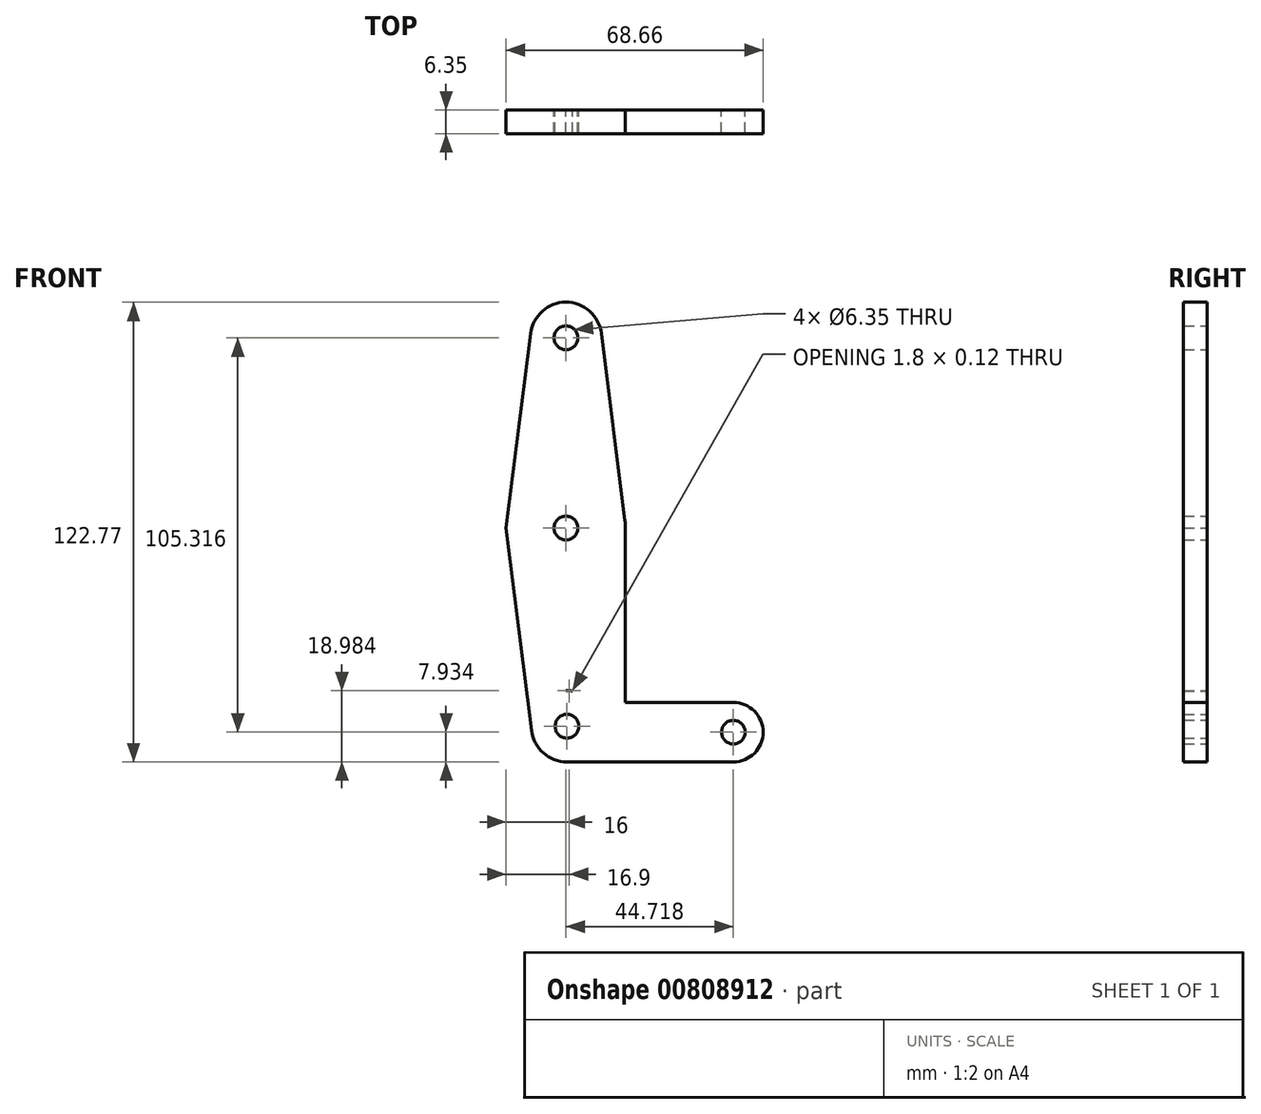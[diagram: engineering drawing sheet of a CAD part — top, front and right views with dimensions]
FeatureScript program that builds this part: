
annotation { "Feature Type Name" : "Feature", "Feature Type Description" : "" }
export const myFeature = defineFeature(function(context is Context, id is Id, definition is map)
    precondition{}
    {
        {
            var Q0;
            Q0=qCreatedBy(makeId("Front.planeOp"),FACE);
            var sketch = newSketch(context, id + "F0", { "sketchPlane" : qUnion([Q0])});
            skCircle(sketch, "E0", {"center": v(0, 0) * mm, "radius": 3.18 * mm});
            skCircle(sketch, "E1", {"center": v(0, 0) * mm, "radius": 15.88 * mm});
            skCircle(sketch, "E2", {"center": v(0, 50.8) * mm, "radius": 3.18 * mm});
            skCircle(sketch, "E3", {"center": v(0, 50.8) * mm, "radius": 9.53 * mm});
            skLineSegment(sketch, "E4", {"start": v(-9.45, 52) * mm, "end": v(-16, 0) * mm});
            skLineSegment(sketch, "E5", {"start": v(7.94, -63.62) * mm, "end": v(8, -63.62) * mm});
            skCircle(sketch, "E6", {"center": v(44.72, -54.52) * mm, "radius": 7.94 * mm});
            skPoint(sketch, "E7.trimOffspring.end.orphan", {"position": v(46.33, -54.52) * mm});
            skPoint(sketch, "E8.trimOffspring.end.orphan", {"position": v(15.88, -63.3) * mm});
            skPoint(sketch, "E9.start.orphan", {"position": v(0, -73.14) * mm});
            skPoint(sketch, "E10.orphan", {"position": v(44.55, -73.14) * mm});
            skPoint(sketch, "E11.end.orphan", {"position": v(9.62, 50.8) * mm});
            skPoint(sketch, "E12.start.orphan", {"position": v(0, -71.55) * mm});
            skPoint(sketch, "E13.start.orphan", {"position": v(14.28, -63.3) * mm});
            skPoint(sketch, "E14.start.orphan", {"position": v(44.55, -71.55) * mm});
            skCircle(sketch, "E15", {"center": v(0.27, -52.93) * mm, "radius": 9.53 * mm});
            skLineSegment(sketch, "E16", {"start": v(-16, 0) * mm, "end": v(-9.18, -54.12) * mm});
            skLineSegment(sketch, "E17", {"start": v(15.88, 0) * mm, "end": v(15.88, -46.58) * mm});
            skLineSegment(sketch, "E18", {"start": v(0, -43.4) * mm, "end": v(1.8, -43.53) * mm});
            skPoint(sketch, "E19.newPointA", {"position": v(15.88, -63.04) * mm});
            skPoint(sketch, "E20.endSnap0", {"position": v(22.28, -72.35) * mm});
            skPoint(sketch, "E20.end.orphan", {"position": v(46.33, -72.35) * mm});
            skLineSegment(sketch, "E21", {"start": v(15.75, 1.98) * mm, "end": v(15.87, 1) * mm});
            skLineSegment(sketch, "E22", {"start": v(0.27, -62.45) * mm, "end": v(44.72, -62.45) * mm});
            skLineSegment(sketch, "E23", {"start": v(9.45, 52) * mm, "end": v(15.75, 1.98) * mm});
            skPoint(sketch, "E24.end.orphan", {"position": v(0, -3.18) * mm});
            skPoint(sketch, "E25.start.orphan", {"position": v(0, -15.88) * mm});
            skCircle(sketch, "E26", {"center": v(0.27, -52.93) * mm, "radius": 3.18 * mm});
            skCircle(sketch, "E27", {"center": v(44.72, -54.52) * mm, "radius": 3.18 * mm});
            skLineSegment(sketch, "E28", {"start": v(0, 50.8) * mm, "end": v(0, 0) * mm});
            skLineSegment(sketch, "E29", {"start": v(15.88, -46.58) * mm, "end": v(44.72, -46.58) * mm});
            skSolve(sketch);
        }
        {
            var Q0;
            Q0 = qSketchRegion(id + "F0", true);
            extrude(context, id + "F1", {"entities" : qUnion([Q0]), "depth" : 6.35 * mm, "offsetDistance" : 25.4 * mm});
        }
        {
            var Q0;
            Q0=sQuery(id+"F0.wireOp",EDGE,"E1");
            extrude(context, id + "F2", {"bodyType" : ToolBodyType.SURFACE, "surfaceEntities" : qUnion([Q0]), "depth" : 25.4 * mm, "offsetDistance" : 25.4 * mm});
        }
        {
            var Q0;
            Q0=sQuery(id+"F0.wireOp",EDGE,"E15");
            extrude(context, id + "F3", {"bodyType" : ToolBodyType.SURFACE, "surfaceEntities" : qUnion([Q0]), "depth" : 31.75 * mm, "offsetDistance" : 25.4 * mm});
        }
        {
            var Q0;
            Q0=sQuery(id+"F0.wireOp",EDGE,"E6");
            extrude(context, id + "F4", {"bodyType" : ToolBodyType.SURFACE, "surfaceEntities" : qUnion([Q0]), "depth" : 31.75 * mm, "offsetDistance" : 25.4 * mm});
        }
        {
            var Q0;
            Q0=sQuery(id+"F0.wireOp",EDGE,"E2");
            extrude(context, id + "F5", {"bodyType" : ToolBodyType.SURFACE, "surfaceEntities" : qUnion([Q0]), "depth" : 31.75 * mm, "offsetDistance" : 25.4 * mm});
        }
        {
            var Q0;
            Q0=sQuery(id+"F0.wireOp",EDGE,"E0");
            extrude(context, id + "F6", {"bodyType" : ToolBodyType.SURFACE, "surfaceEntities" : qUnion([Q0]), "depth" : 31.75 * mm, "offsetDistance" : 25.4 * mm});
        }
        {
            var Q0;
            Q0=sQuery(id+"F0.wireOp",EDGE,"E0");
            extrude(context, id + "F7", {"bodyType" : ToolBodyType.SURFACE, "surfaceOperationType" : NewSurfaceOperationType.ADD, "surfaceEntities" : qUnion([Q0]), "depth" : 25.4 * mm, "offsetDistance" : 25.4 * mm});
        }
    });
